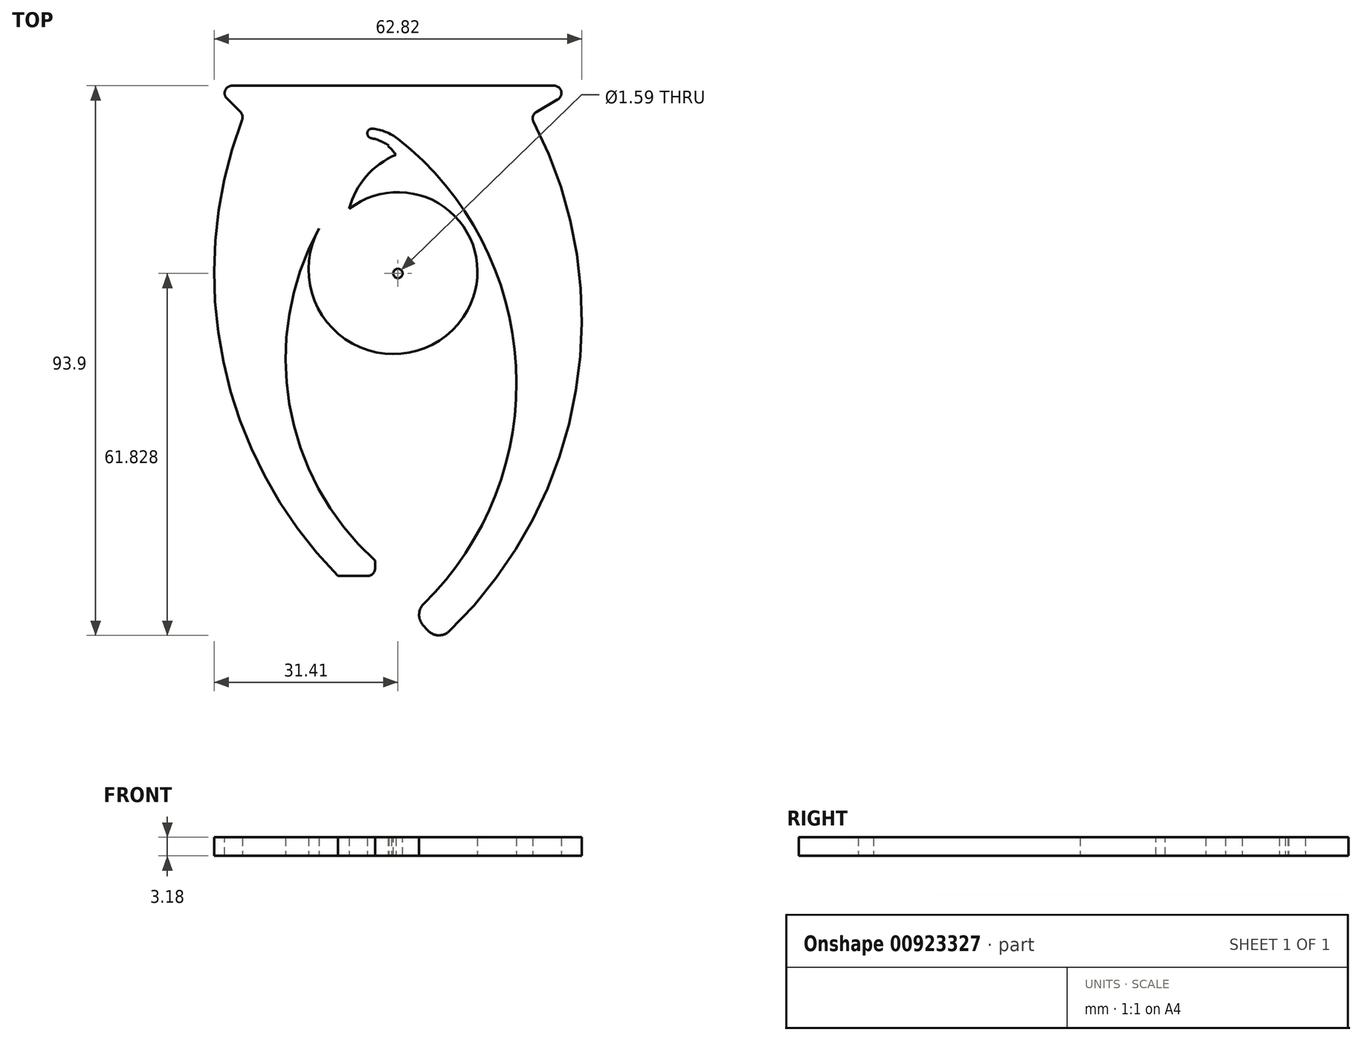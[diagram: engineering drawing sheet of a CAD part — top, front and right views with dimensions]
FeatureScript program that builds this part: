
annotation { "Feature Type Name" : "Feature", "Feature Type Description" : "" }
export const myFeature = defineFeature(function(context is Context, id is Id, definition is map)
    precondition{}
    {
        {
            var Q0;
            Q0=qCreatedBy(makeId("Top.planeOp"),FACE);
            var sketch = newSketch(context, id + "F0", { "sketchPlane" : qUnion([Q0])});
            skLineSegment(sketch, "E0.bottom", {"start": v(-76.2, 101.6) * mm, "end": v(76.2, 101.6) * mm});
            skLineSegment(sketch, "E0.top", {"start": v(-76.2, -101.6) * mm, "end": v(76.2, -101.6) * mm});
            skLineSegment(sketch, "E0.left", {"start": v(-76.2, 101.6) * mm, "end": v(-76.2, -101.6) * mm});
            skLineSegment(sketch, "E0.right", {"start": v(76.2, 101.6) * mm, "end": v(76.2, -101.6) * mm});
            skLineSegment(sketch, "E1", {"start": v(-76.2, 101.6) * mm, "end": v(76.2, -101.6) * mm, "construction": true});
            skSolve(sketch);
        }
        {
            var Q0;
            Q0=makeQuery(id+"F0.imprint","IMPRINT",FACE,{"disambiguationData":[TD([[makeQuery(id+"F0.imprint","IMPRINT",EDGE,{"derivedFrom":sQuery(id+"F0.wireOp",EDGE,"E0.bottom")}),-1.0]])]});
            var sketch = newSketch(context, id + "F1", { "sketchPlane" : qUnion([Q0])});
            skLineSegment(sketch, "E2", {"start": v(-31.4, 31.78) * mm, "end": v(31.4, 31.78) * mm});
            skCircle(sketch, "E3", {"center": v(0, 0) * mm, "radius": 13.6 * mm});
            skLineSegment(sketch, "E4", {"start": v(-13.6, 0) * mm, "end": v(13.6, 0) * mm, "construction": true});
            skLineSegment(sketch, "E5", {"start": v(13.6, 0) * mm, "end": v(40.78, 0) * mm, "construction": true});
            skLineSegment(sketch, "E6", {"start": v(0, 0) * mm, "end": v(0, 31.78) * mm, "construction": true});
            skLineSegment(sketch, "E7", {"start": v(31.4, 31.78) * mm, "end": v(22.6, 26.7) * mm});
            skLineSegment(sketch, "E8", {"start": v(-31.4, 31.78) * mm, "end": v(-26.33, 26.7) * mm});
            skArc(sketch, "E9", {"start": v(-26.33, 26.7) * mm, "mid": v(-29.4, -17.31) * mm, "end": v(-6.84, -55.23) * mm});
            skLineSegment(sketch, "E10", {"start": v(-31.4, 31.78) * mm, "end": v(-31.4, -0.22) * mm, "construction": true});
            skArc(sketch, "E11", {"start": v(6.84, -63.2) * mm, "mid": v(30.3, -20.98) * mm, "end": v(22.6, 26.7) * mm});
            skLineSegment(sketch, "E12", {"start": v(31.4, 31.78) * mm, "end": v(31.4, -8.23) * mm, "construction": true});
            skLineSegment(sketch, "E13", {"start": v(-26.33, 26.7) * mm, "end": v(22.6, 26.7) * mm, "construction": true});
            skLineSegment(sketch, "E14", {"start": v(-6.84, -49.73) * mm, "end": v(-6.84, -55.23) * mm, "construction": true});
            skLineSegment(sketch, "E15", {"start": v(6.84, -63.2) * mm, "end": v(6.84, -49.73) * mm, "construction": true});
            skLineSegment(sketch, "E16", {"start": v(6.84, -63.2) * mm, "end": v(2.6, -58.47) * mm});
            skLineSegment(sketch, "E17", {"start": v(-6.84, -55.23) * mm, "end": v(-2.6, -50.5) * mm});
            skArc(sketch, "E18", {"start": v(2.6, -58.47) * mm, "mid": v(20.23, -17.28) * mm, "end": v(0, 22.69) * mm});
            skLineSegment(sketch, "E19", {"start": v(0, 13.6) * mm, "end": v(0, 31.78) * mm, "construction": true});
            skArc(sketch, "E20", {"start": v(0, 22.69) * mm, "mid": v(-19.17, -13.27) * mm, "end": v(-2.6, -50.5) * mm});
            skLineSegment(sketch, "E21", {"start": v(2.6, -58.47) * mm, "end": v(2.6, -13.34) * mm, "construction": true});
            skLineSegment(sketch, "E22", {"start": v(2.6, -13.34) * mm, "end": v(2.6, 31.78) * mm, "construction": true});
            skLineSegment(sketch, "E23", {"start": v(-16.74, 0) * mm, "end": v(-13.6, 0) * mm, "construction": true});
            skLineSegment(sketch, "E24", {"start": v(13.6, 0) * mm, "end": v(16.74, 0) * mm, "construction": true});
            skSolve(sketch);
        }
        {
            var Q0;
            Q0 = qSketchRegion(id + "F1", true);
            extrude(context, id + "F2", {"entities" : qUnion([Q0]), "depth" : 3.17 * mm, "offsetDistance" : 25.4 * mm});
        }
        {
            var Q0;
            Q0=makeQuery(id+"F0.imprint","IMPRINT",FACE,{"disambiguationData":[TD([[makeQuery(id+"F0.imprint","IMPRINT",EDGE,{"derivedFrom":sQuery(id+"F0.wireOp",EDGE,"E0.bottom")}),-1.0]])]});
            var sketch = newSketch(context, id + "F3", { "sketchPlane" : qUnion([Q0])});
            skArc(sketch, "E25", {"start": v(-13.49, 7.39) * mm, "mid": v(-7.74, -12.28) * mm, "end": v(11.92, -6.53) * mm});
            skLineSegment(sketch, "E26", {"start": v(0, 0) * mm, "end": v(11.92, -6.53) * mm, "construction": true});
            skArc(sketch, "E27", {"start": v(0, 20.1) * mm, "mid": v(-7.84, 2.47) * mm, "end": v(9.8, -5.36) * mm});
            skLineSegment(sketch, "E28", {"start": v(0, 22.69) * mm, "end": v(-4, 25.83) * mm, "construction": true});
            skLineSegment(sketch, "E29", {"start": v(0, 20.1) * mm, "end": v(-5.25, 24.23) * mm});
            skLineSegment(sketch, "E30", {"start": v(-5.25, 24.23) * mm, "end": v(-4, 25.83) * mm, "construction": true});
            skLineSegment(sketch, "E31", {"start": v(-13.49, 7.39) * mm, "end": v(-5.25, 24.23) * mm});
            skLineSegment(sketch, "E32", {"start": v(9.8, -5.36) * mm, "end": v(11.92, -6.53) * mm});
            skSolve(sketch);
        }
        {
            var Q0;
            Q0 = qSketchRegion(id + "F3", true);
            var Q1;
            Q1=makeQuery(id+"F2.opExtrude","CAP_FACE",FACE,{"disambiguationData":[OSD([sQuery(id+"F1.wireOp",EDGE,"E2"),sQuery(id+"F1.wireOp",EDGE,"E7"),sQuery(id+"F1.wireOp",EDGE,"E8"),sQuery(id+"F1.wireOp",EDGE,"E9"),sQuery(id+"F1.wireOp",EDGE,"E11"),sQuery(id+"F1.wireOp",EDGE,"E16"),sQuery(id+"F1.wireOp",EDGE,"E17"),sQuery(id+"F1.wireOp",EDGE,"E18"),sQuery(id+"F1.wireOp",EDGE,"E20")])],"isStart":false});
            extrude(context, id + "F4", {"entities" : qUnion([Q0]), "operationType" : NewBodyOperationType.ADD, "endBound" : BoundingType.UP_TO_SURFACE, "depth" : 2.54 * mm, "endBoundEntityFace" : qUnion([Q1]), "offsetDistance" : 25.4 * mm});
        }
        {
            var Q0;
            Q0=makeQuery(id+"F0.imprint","IMPRINT",FACE,{"disambiguationData":[TD([[makeQuery(id+"F0.imprint","IMPRINT",EDGE,{"derivedFrom":sQuery(id+"F0.wireOp",EDGE,"E0.bottom")}),-1.0]])]});
            var sketch = newSketch(context, id + "F5", { "sketchPlane" : qUnion([Q0])});
            skLineSegment(sketch, "E33", {"start": v(-3.9, -51.96) * mm, "end": v(-10.26, -51.96) * mm});
            skLineSegment(sketch, "E34", {"start": v(-3.9, -51.96) * mm, "end": v(-3.9, -49.36) * mm});
            skLineSegment(sketch, "E35", {"start": v(-10.26, -51.96) * mm, "end": v(-10.26, -62.68) * mm});
            skLineSegment(sketch, "E36", {"start": v(-10.26, -62.68) * mm, "end": v(0, -56.92) * mm});
            skLineSegment(sketch, "E37", {"start": v(0, -56.92) * mm, "end": v(-2.61, -45.9) * mm});
            skLineSegment(sketch, "E38", {"start": v(-2.61, -45.9) * mm, "end": v(-3.9, -49.36) * mm});
            skLineSegment(sketch, "E39", {"start": v(0, 22.69) * mm, "end": v(0, 19.5) * mm});
            skArc(sketch, "E40", {"start": v(0, 22.69) * mm, "mid": v(-2.52, 24.05) * mm, "end": v(-5.36, 24.46) * mm});
            skLineSegment(sketch, "E41", {"start": v(0, 19.5) * mm, "end": v(-1.52, 21.54) * mm});
            skArc(sketch, "E42", {"start": v(-1.52, 21.54) * mm, "mid": v(-3.24, 22.44) * mm, "end": v(-5.12, 22.92) * mm});
            skLineSegment(sketch, "E43", {"start": v(-5.36, 24.46) * mm, "end": v(-5.12, 22.92) * mm});
            skSolve(sketch);
        }
        {
            var Q0;
            Q0 = qSketchRegion(id + "F5", true);
            var Q1;
            Q1=makeQuery(id+"F2.opExtrude","CAP_FACE",FACE,{"disambiguationData":[OSD([sQuery(id+"F1.wireOp",EDGE,"E2"),sQuery(id+"F1.wireOp",EDGE,"E7"),sQuery(id+"F1.wireOp",EDGE,"E8"),sQuery(id+"F1.wireOp",EDGE,"E9"),sQuery(id+"F1.wireOp",EDGE,"E11"),sQuery(id+"F1.wireOp",EDGE,"E16"),sQuery(id+"F1.wireOp",EDGE,"E17"),sQuery(id+"F1.wireOp",EDGE,"E18"),sQuery(id+"F1.wireOp",EDGE,"E20")])],"isStart":false});
            extrude(context, id + "F6", {"entities" : qUnion([Q0]), "operationType" : NewBodyOperationType.REMOVE, "endBound" : BoundingType.UP_TO_SURFACE, "depth" : 25.4 * mm, "endBoundEntityFace" : qUnion([Q1]), "offsetDistance" : 25.4 * mm});
        }
        {
            var Q0;
            Q0=makeQuery(id+"F2.opExtrude","SWEPT_EDGE",EDGE,{"disambiguationData":[OSD([sQuery(id+"F1.wireOp",EDGE,"E2"),sQuery(id+"F1.wireOp",EDGE,"E8")])]});
            var Q1;
            Q1=makeQuery(id+"F2.opExtrude","SWEPT_EDGE",EDGE,{"disambiguationData":[OSD([sQuery(id+"F1.wireOp",EDGE,"E8"),sQuery(id+"F1.wireOp",EDGE,"E9")])]});
            var Q2;
            Q2=makeQuery(id+"F2.opExtrude","SWEPT_EDGE",EDGE,{"disambiguationData":[OSD([sQuery(id+"F1.wireOp",EDGE,"E2"),sQuery(id+"F1.wireOp",EDGE,"E7")])]});
            var Q3;
            Q3=makeQuery(id+"F2.opExtrude","SWEPT_EDGE",EDGE,{"disambiguationData":[OSD([sQuery(id+"F1.wireOp",EDGE,"E7"),sQuery(id+"F1.wireOp",EDGE,"E11")])]});
            var Q4;
            Q4=makeQuery(id+"F6.boolean.opBoolean","COPY",EDGE,{"derivedFrom":makeQuery(id+"F6.opExtrude","SWEPT_EDGE",EDGE,{"disambiguationData":[OSD([sQuery(id+"F5.wireOp",EDGE,"E34"),sQuery(id+"F5.wireOp",EDGE,"E38")])]})});
            var Q5;
            Q5=makeQuery(id+"F6.boolean.opBoolean","COPY",EDGE,{"derivedFrom":makeQuery(id+"F6.opExtrude","SWEPT_EDGE",EDGE,{"disambiguationData":[OSD([sQuery(id+"F5.wireOp",EDGE,"E33"),sQuery(id+"F5.wireOp",EDGE,"E34")])]})});
            var Q6;
            Q6=makeQuery(id+"F6.boolean.opBoolean","COPY",EDGE,{"derivedFrom":makeQuery(id+"F6.opExtrude","SWEPT_EDGE",EDGE,{"disambiguationData":[OSD([sQuery(id+"F5.wireOp",EDGE,"E33"),sQuery(id+"F5.wireOp",EDGE,"E35")])]})});
            var Q7;
            Q7=makeQuery(id+"F4.opExtrude","SWEPT_EDGE",EDGE,{"disambiguationData":[OSD([sQuery(id+"F3.wireOp",EDGE,"E27"),sQuery(id+"F3.wireOp",EDGE,"E29")])]});
            fillet(context, id + "F7", {"entities" : qUnion([Q0, Q1, Q2, Q3, Q4, Q5, Q6, Q7]), "radius" : 1.27 * mm, "tangentPropagation" : true, "allowEdgeOverflow" : false});
        }
        {
            var Q0;
            Q0=makeQuery(id+"F6.boolean.opBoolean","COPY",EDGE,{"derivedFrom":makeQuery(id+"F6.opExtrude","SWEPT_EDGE",EDGE,{"disambiguationData":[OSD([sQuery(id+"F5.wireOp",EDGE,"E40"),sQuery(id+"F5.wireOp",EDGE,"E43")])]})});
            var Q1;
            Q1=makeQuery(id+"F6.boolean.opBoolean","COPY",EDGE,{"derivedFrom":makeQuery(id+"F6.opExtrude","SWEPT_EDGE",EDGE,{"disambiguationData":[OSD([sQuery(id+"F5.wireOp",EDGE,"E42"),sQuery(id+"F5.wireOp",EDGE,"E43")])]})});
            fillet(context, id + "F8", {"entities" : qUnion([Q0, Q1]), "radius" : 0.76 * mm, "tangentPropagation" : true, "allowEdgeOverflow" : false});
        }
        {
            var Q0;
            Q0=makeQuery(id+"F2.opExtrude","CAP_FACE",FACE,{"disambiguationData":[OSD([sQuery(id+"F1.wireOp",EDGE,"E3")])],"isStart":false});
            var sketch = newSketch(context, id + "F9", { "sketchPlane" : qUnion([Q0])});
            skCircle(sketch, "E44", {"center": v(0, -0.3) * mm, "radius": 0.8 * mm});
            skSolve(sketch);
        }
        {
            var Q0;
            Q0 = qSketchRegion(id + "F9", true);
            extrude(context, id + "F10", {"entities" : qUnion([Q0]), "operationType" : NewBodyOperationType.REMOVE, "endBound" : BoundingType.THROUGH_ALL, "oppositeDirection" : true, "depth" : 25.4 * mm, "offsetDistance" : 25.4 * mm});
        }
        {
            var Q0;
            Q0=makeQuery(id+"F2.opExtrude","SWEPT_EDGE",EDGE,{"disambiguationData":[OSD([sQuery(id+"F1.wireOp",EDGE,"E16"),sQuery(id+"F1.wireOp",EDGE,"E18")])]});
            var Q1;
            Q1=makeQuery(id+"F2.opExtrude","SWEPT_EDGE",EDGE,{"disambiguationData":[OSD([sQuery(id+"F1.wireOp",EDGE,"E11"),sQuery(id+"F1.wireOp",EDGE,"E16")])]});
            fillet(context, id + "F11", {"entities" : qUnion([Q0, Q1]), "radius" : 2.54 * mm, "tangentPropagation" : true, "allowEdgeOverflow" : false});
        }
    });
